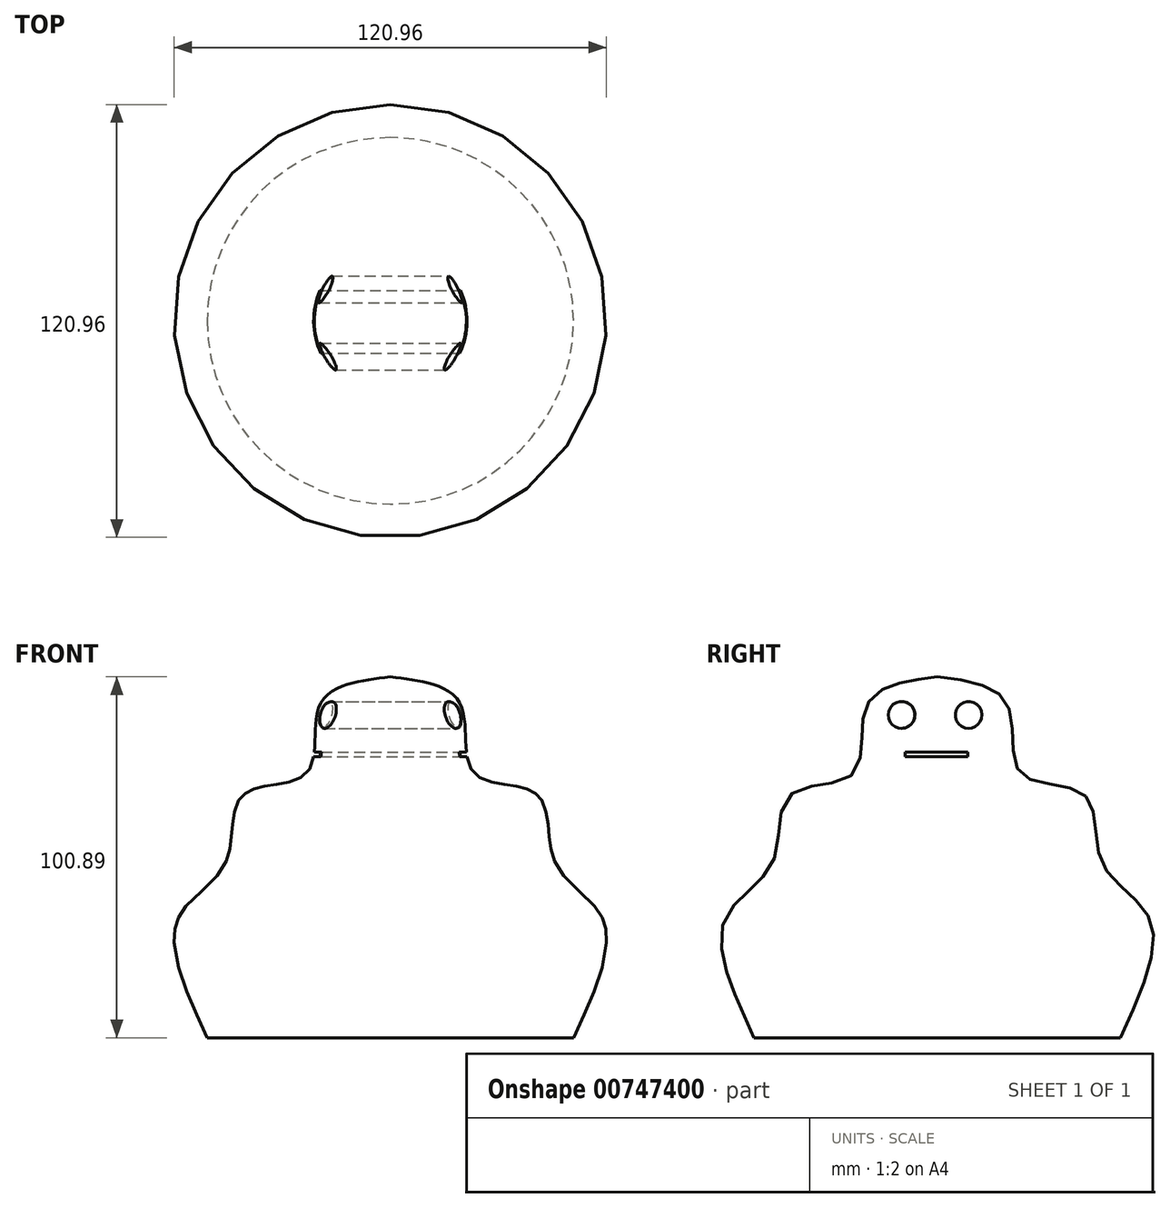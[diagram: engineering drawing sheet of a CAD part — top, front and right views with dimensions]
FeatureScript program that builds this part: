
annotation { "Feature Type Name" : "Feature", "Feature Type Description" : "" }
export const myFeature = defineFeature(function(context is Context, id is Id, definition is map)
    precondition{}
    {
        {
            var Q0;
            Q0=qCreatedBy(makeId("Right.planeOp"),FACE);
            var sketch = newSketch(context, id + "F0", { "sketchPlane" : qUnion([Q0])});
            skLineSegment(sketch, "E0", {"start": v(0, 0) * mm, "end": v(51.23, 0) * mm});
            skLineSegment(sketch, "E1", {"start": v(0, 0) * mm, "end": v(0, 100.9) * mm});
            skFitSpline(sketch, "E2", {"points": [v(0, 100.9) * mm, v(19.66, 93.14) * mm, v(23.4, 73.9) * mm, v(41.19, 67.88) * mm, v(46.07, 48.94) * mm, v(59.56, 32.86) * mm, v(51.23, 0) * mm], "startDerivative": vector(155.78, -19.15) * mm, "endDerivative": vector(-83.73, -181.14) * mm});
            skSolve(sketch);
        }
        {
            var Q0;
            Q0=makeQuery(id+"F0.imprint","IMPRINT",FACE,{"disambiguationData":[TD([[makeQuery(id+"F0.imprint","IMPRINT",EDGE,{"derivedFrom":sQuery(id+"F0.wireOp",EDGE,"E0")}),1.0]])]});
            var Q1;
            Q1=sQuery(id+"F0.wireOp",EDGE,"E1");
            revolve(context, id + "F1", {"surfaceOperationType" : NewSurfaceOperationType.NEW, "entities" : qUnion([Q0]), "axis" : qUnion([Q1]), "revolveType" : RevolveType.FULL});
        }
        {
            var Q0;
            Q0=qCreatedBy(makeId("Right.planeOp"),FACE);
            cPlane(context, id + "F2", {"entities" : qUnion([Q0]), "cplaneType" : CPlaneType.OFFSET, "offset" : 25 * mm, "width" : 150 * mm, "height" : 150 * mm});
        }
        {
            var Q0;
            Q0=qCreatedBy(id+"F2.planeOp",FACE);
            var sketch = newSketch(context, id + "F3", { "sketchPlane" : qUnion([Q0])});
            skCircle(sketch, "E3", {"center": v(-9.98, 90.22) * mm, "radius": 3.75 * mm});
            skCircle(sketch, "E4", {"center": v(8.77, 90.22) * mm, "radius": 3.75 * mm});
            skLineSegment(sketch, "E5", {"start": v(0, 79.86) * mm, "end": v(8.55, 79.86) * mm});
            skLineSegment(sketch, "E6", {"start": v(0, 79.86) * mm, "end": v(-9.04, 79.86) * mm});
            skLineSegment(sketch, "E7", {"start": v(-9.04, 79.86) * mm, "end": v(-9.04, 78.52) * mm});
            skLineSegment(sketch, "E8", {"start": v(-9.04, 78.52) * mm, "end": v(8.55, 78.52) * mm});
            skLineSegment(sketch, "E9", {"start": v(8.55, 78.52) * mm, "end": v(8.55, 79.86) * mm});
            skLineSegment(sketch, "E10", {"start": v(0, 0) * mm, "end": v(0, 107.42) * mm, "construction": true});
            skLineSegment(sketch, "E11", {"start": v(-9.98, 90.22) * mm, "end": v(8.77, 90.22) * mm, "construction": true});
            skSolve(sketch);
        }
        {
            var Q0;
            Q0 = qSketchRegion(id + "F3", true);
            extrude(context, id + "F4", {"entities" : qUnion([Q0]), "operationType" : NewBodyOperationType.REMOVE, "endBound" : BoundingType.THROUGH_ALL, "oppositeDirection" : true, "depth" : 25 * mm, "offsetDistance" : 25 * mm});
        }
    });
